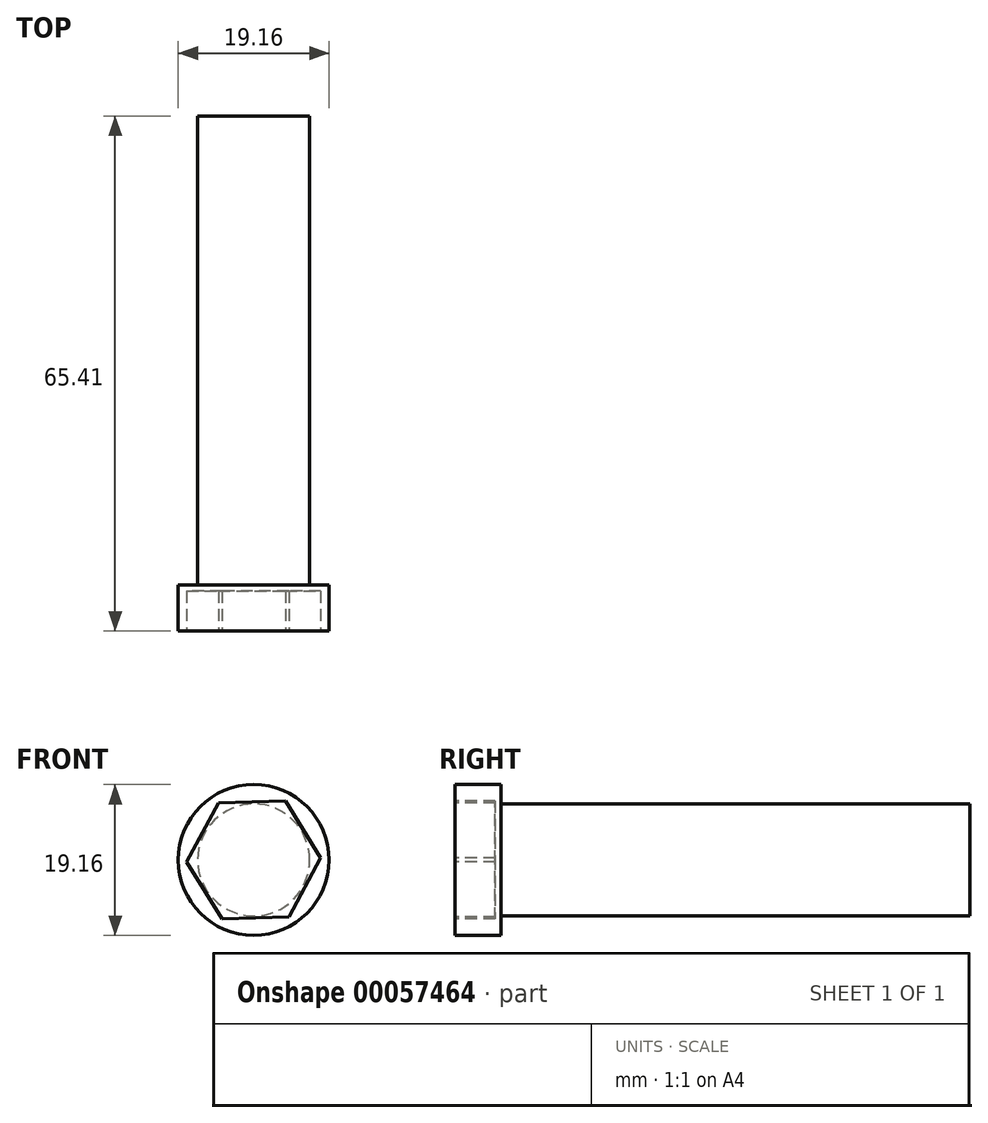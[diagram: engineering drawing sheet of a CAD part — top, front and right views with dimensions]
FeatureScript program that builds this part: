
annotation { "Feature Type Name" : "Feature", "Feature Type Description" : "" }
export const myFeature = defineFeature(function(context is Context, id is Id, definition is map)
    precondition{}
    {
        {
            var Q0;
            Q0=qCreatedBy(makeId("Front.planeOp"),FACE);
            var sketch = newSketch(context, id + "F0", { "sketchPlane" : qUnion([Q0])});
            skCircle(sketch, "E0", {"center": v(0, 0) * mm, "radius": 7.11 * mm});
            skSolve(sketch);
        }
        {
            var Q0;
            Q0=makeQuery(id+"F0.imprint","IMPRINT",FACE,{"disambiguationData":[TD([[makeQuery(id+"F0.imprint","IMPRINT",EDGE,{"derivedFrom":sQuery(id+"F0.wireOp",EDGE,"E0")}),1.0]])]});
            extrude(context, id + "F1", {"entities" : qUnion([Q0]), "depth" : 59.56 * mm});
        }
        {
            var Q0;
            Q0=makeQuery(id+"F1.opExtrude","CAP_FACE",FACE,{"disambiguationData":[OSD([sQuery(id+"F0.wireOp",EDGE,"E0")])],"isStart":false});
            var sketch = newSketch(context, id + "F2", { "sketchPlane" : qUnion([Q0])});
            skCircle(sketch, "E1", {"center": v(0, 0) * mm, "radius": 9.58 * mm});
            skSolve(sketch);
        }
        {
            var Q0;
            Q0=makeQuery(id+"F2.imprint","IMPRINT",FACE,{"disambiguationData":[TD([[makeQuery(id+"F2.imprint","IMPRINT",EDGE,{"derivedFrom":makeQuery(id+"F1.opExtrude","CAP_EDGE",EDGE,{"disambiguationData":[OSD([sQuery(id+"F0.wireOp",EDGE,"E0")])],"isStart":false})}),1.0]])]});
            var Q1;
            Q1=makeQuery(id+"F2.imprint","IMPRINT",FACE,{"disambiguationData":[TD([[makeQuery(id+"F2.imprint","IMPRINT",EDGE,{"derivedFrom":sQuery(id+"F2.wireOp",EDGE,"E1")}),1.0]])]});
            extrude(context, id + "F3", {"entities" : qUnion([Q0, Q1]), "operationType" : NewBodyOperationType.ADD, "depth" : 5.84 * mm});
        }
        {
            var Q0;
            Q0=makeQuery(id+"F3.opExtrude","CAP_FACE",FACE,{"disambiguationData":[OSD([sQuery(id+"F2.wireOp",EDGE,"E1")])],"isStart":false});
            var sketch = newSketch(context, id + "F4", { "sketchPlane" : qUnion([Q0])});
            skCircle(sketch, "E2.cCircle", {"center": v(0, 0) * mm, "radius": 8.5 * mm, "construction": true});
            skLineSegment(sketch, "E2.0", {"start": v(4.03, 7.5) * mm, "end": v(8.5, 0.26) * mm});
            skLineSegment(sketch, "E2.1", {"start": v(8.5, 0.26) * mm, "end": v(4.47, -7.24) * mm});
            skLineSegment(sketch, "E2.2", {"start": v(4.47, -7.24) * mm, "end": v(-4.03, -7.5) * mm});
            skLineSegment(sketch, "E2.3", {"start": v(-4.03, -7.5) * mm, "end": v(-8.5, -0.26) * mm});
            skLineSegment(sketch, "E2.4", {"start": v(-8.5, -0.26) * mm, "end": v(-4.47, 7.24) * mm});
            skLineSegment(sketch, "E2.5", {"start": v(-4.47, 7.24) * mm, "end": v(4.03, 7.5) * mm});
            skSolve(sketch);
        }
        {
            var Q0;
            Q0=makeQuery(id+"F4.imprint","IMPRINT",FACE,{"disambiguationData":[TD([[makeQuery(id+"F4.imprint","IMPRINT",EDGE,{"derivedFrom":sQuery(id+"F4.wireOp",EDGE,"E2.0")}),-1.0]])]});
            extrude(context, id + "F5", {"entities" : qUnion([Q0]), "operationType" : NewBodyOperationType.REMOVE, "oppositeDirection" : true, "depth" : 5.08 * mm});
        }
    });
